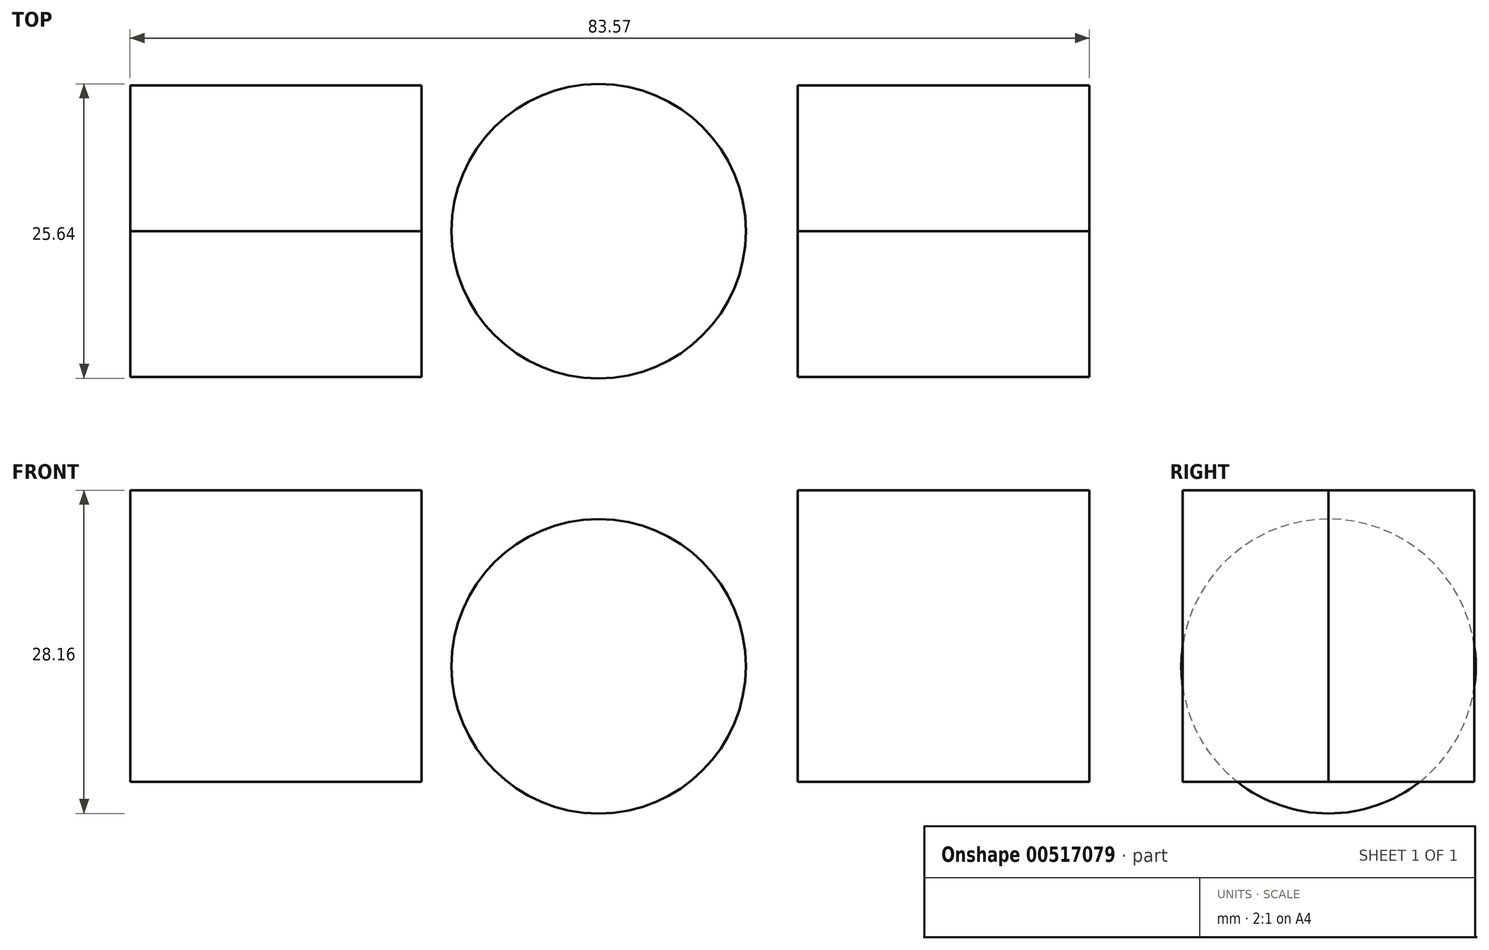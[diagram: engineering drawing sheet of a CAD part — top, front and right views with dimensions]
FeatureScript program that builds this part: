
annotation { "Feature Type Name" : "Feature", "Feature Type Description" : "" }
export const myFeature = defineFeature(function(context is Context, id is Id, definition is map)
    precondition{}
    {
        {
            var Q0;
            Q0=qCreatedBy(makeId("Front.planeOp"),FACE);
            var sketch = newSketch(context, id + "F0", { "sketchPlane" : qUnion([Q0])});
            skLineSegment(sketch, "E0.bottom", {"start": v(-62.67, 15.34) * mm, "end": v(-37.27, 15.34) * mm});
            skLineSegment(sketch, "E0.top", {"start": v(-62.67, -10.06) * mm, "end": v(-37.27, -10.06) * mm});
            skLineSegment(sketch, "E0.left", {"start": v(-62.67, 15.34) * mm, "end": v(-62.67, -10.06) * mm});
            skLineSegment(sketch, "E0.right", {"start": v(-37.27, 15.34) * mm, "end": v(-37.27, -10.06) * mm});
            skLineSegment(sketch, "E1.bottom", {"start": v(-4.5, 15.34) * mm, "end": v(20.9, 15.34) * mm});
            skLineSegment(sketch, "E1.top", {"start": v(-4.5, -10.06) * mm, "end": v(20.9, -10.06) * mm});
            skLineSegment(sketch, "E1.left", {"start": v(-4.5, 15.34) * mm, "end": v(-4.5, -10.06) * mm});
            skLineSegment(sketch, "E1.right", {"start": v(20.9, 15.34) * mm, "end": v(20.9, -10.06) * mm});
            skLineSegment(sketch, "E2", {"start": v(-9.04, 0) * mm, "end": v(-34.69, 0) * mm});
            skArc(sketch, "E3", {"start": v(-9.04, 0) * mm, "mid": v(-21.86, 12.82) * mm, "end": v(-34.69, 0) * mm});
            skLineSegment(sketch, "E4.bottom", {"start": v(20.9, 12.68) * mm, "end": v(40.14, 12.68) * mm});
            skLineSegment(sketch, "E4.top", {"start": v(20.9, -7.72) * mm, "end": v(40.14, -7.72) * mm});
            skLineSegment(sketch, "E4.left", {"start": v(20.9, 12.68) * mm, "end": v(20.9, -7.72) * mm});
            skLineSegment(sketch, "E4.right", {"start": v(40.14, 12.68) * mm, "end": v(40.14, -7.72) * mm});
            skLineSegment(sketch, "E5.bottom", {"start": v(40.14, 9.76) * mm, "end": v(54.71, 9.76) * mm});
            skLineSegment(sketch, "E5.top", {"start": v(40.14, -4.52) * mm, "end": v(54.71, -4.52) * mm});
            skLineSegment(sketch, "E5.left", {"start": v(40.14, 9.76) * mm, "end": v(40.14, -4.52) * mm});
            skLineSegment(sketch, "E5.right", {"start": v(54.71, 9.76) * mm, "end": v(54.71, -4.52) * mm});
            skSolve(sketch);
        }
        {
            var Q0;
            Q0=makeQuery(id+"F0.imprint","IMPRINT",FACE,{"disambiguationData":[TD([[makeQuery(id+"F0.imprint","IMPRINT",EDGE,{"derivedFrom":sQuery(id+"F0.wireOp",EDGE,"E0.bottom")}),-1.0]])]});
            var Q1;
            Q1=makeQuery(id+"F0.imprint","IMPRINT",FACE,{"disambiguationData":[TD([[makeQuery(id+"F0.imprint","IMPRINT",EDGE,{"derivedFrom":sQuery(id+"F0.wireOp",EDGE,"E1.bottom")}),-1.0]])]});
            extrude(context, id + "F1", {"entities" : qUnion([Q0, Q1]), "depth" : 12.7 * mm, "offsetDistance" : 25.4 * mm});
        }
        {
            var Q0;
            Q0=makeQuery(id+"F0.imprint","IMPRINT",FACE,{"disambiguationData":[TD([[makeQuery(id+"F0.imprint","IMPRINT",EDGE,{"derivedFrom":sQuery(id+"F0.wireOp",EDGE,"E2")}),-1.0]])]});
            var Q1;
            Q1=sQuery(id+"F0.wireOp",EDGE,"E2");
            revolve(context, id + "F2", {"entities" : qUnion([Q0]), "axis" : qUnion([Q1]), "revolveType" : RevolveType.FULL});
        }
        {
            var Q0;
            Q0=makeQuery(id+"F1.opExtrude","CAP_FACE",FACE,{"disambiguationData":[OSD([sQuery(id+"F0.wireOp",EDGE,"E1.bottom"),sQuery(id+"F0.wireOp",EDGE,"E1.top"),sQuery(id+"F0.wireOp",EDGE,"E1.left"),sQuery(id+"F0.wireOp",EDGE,"E1.right")])],"isStart":true});
            var Q1;
            Q1=makeQuery(id+"F1.opExtrude","CAP_FACE",FACE,{"disambiguationData":[OSD([sQuery(id+"F0.wireOp",EDGE,"E0.bottom"),sQuery(id+"F0.wireOp",EDGE,"E0.top"),sQuery(id+"F0.wireOp",EDGE,"E0.left"),sQuery(id+"F0.wireOp",EDGE,"E0.right")])],"isStart":true});
            extrude(context, id + "F3", {"entities" : qUnion([Q0, Q1]), "depth" : 12.7 * mm, "offsetDistance" : 25.4 * mm});
        }
    });
